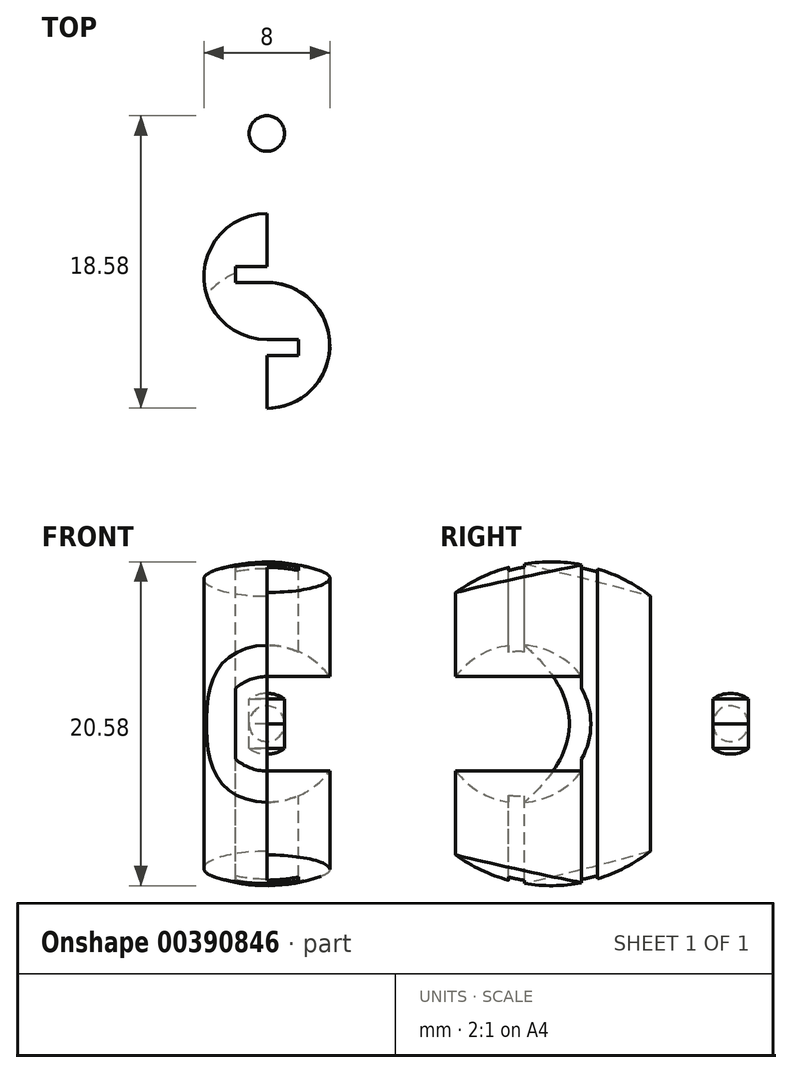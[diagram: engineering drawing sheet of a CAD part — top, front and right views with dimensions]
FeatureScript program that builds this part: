
annotation { "Feature Type Name" : "Feature", "Feature Type Description" : "" }
export const myFeature = defineFeature(function(context is Context, id is Id, definition is map)
    precondition{}
    {
        {
            var Q0;
            Q0=qCreatedBy(makeId("Top.planeOp"),FACE);
            var sketch = newSketch(context, id + "F0", { "sketchPlane" : qUnion([Q0])});
            skLineSegment(sketch, "E0", {"start": v(0, 51.88) * mm, "end": v(0, 12.79) * mm});
            skLineSegment(sketch, "E1", {"start": v(81.06, 0) * mm, "end": v(-86.12, 0) * mm, "construction": true});
            skArc(sketch, "E2", {"start": v(0, 12.79) * mm, "mid": v(-5, 7.79) * mm, "end": v(0, 2.79) * mm});
            skArc(sketch, "E3", {"start": v(0, 11.79) * mm, "mid": v(-4, 7.79) * mm, "end": v(0, 3.79) * mm});
            skArc(sketch, "E4", {"start": v(0, -1.57) * mm, "mid": v(5, 3.43) * mm, "end": v(0, 8.43) * mm});
            skArc(sketch, "E5.trimOffspring", {"start": v(0, -0.57) * mm, "mid": v(4, 3.43) * mm, "end": v(0, 7.43) * mm});
            skLineSegment(sketch, "E6", {"start": v(0, 11.79) * mm, "end": v(2, 11.79) * mm});
            skLineSegment(sketch, "E7", {"start": v(2, 11.79) * mm, "end": v(2, 12.79) * mm});
            skLineSegment(sketch, "E8", {"start": v(2, 12.79) * mm, "end": v(0, 12.79) * mm});
            skLineSegment(sketch, "E9", {"start": v(0, 3.79) * mm, "end": v(2, 3.79) * mm});
            skLineSegment(sketch, "E10", {"start": v(2, 3.79) * mm, "end": v(2, 2.79) * mm});
            skLineSegment(sketch, "E11", {"start": v(2, 2.79) * mm, "end": v(0, 2.79) * mm});
            skLineSegment(sketch, "E12", {"start": v(-2, 8.43) * mm, "end": v(0, 8.43) * mm});
            skLineSegment(sketch, "E13", {"start": v(-2, 8.43) * mm, "end": v(-2, 7.43) * mm});
            skLineSegment(sketch, "E14", {"start": v(0, 7.43) * mm, "end": v(-2, 7.43) * mm});
            skLineSegment(sketch, "E15", {"start": v(0, -0.57) * mm, "end": v(-2, -0.57) * mm});
            skLineSegment(sketch, "E16", {"start": v(-2, -0.57) * mm, "end": v(-2, -1.57) * mm});
            skLineSegment(sketch, "E17", {"start": v(0, -1.57) * mm, "end": v(-2, -1.57) * mm});
            skPoint(sketch, "E18.middle", {"position": v(0, 5.45) * mm});
            skArc(sketch, "E19", {"start": v(-1.47, 15.63) * mm, "mid": v(0, -4.83) * mm, "end": v(1.47, 15.63) * mm});
            skLineSegment(sketch, "E20.trimOffspring", {"start": v(0, 11.79) * mm, "end": v(0, 8.43) * mm});
            skLineSegment(sketch, "E21.trimOffspring", {"start": v(0, 7.43) * mm, "end": v(0, 3.79) * mm});
            skLineSegment(sketch, "E22.trimOffspring", {"start": v(0, 2.79) * mm, "end": v(0, -0.57) * mm});
            skLineSegment(sketch, "E23.trimOffspring", {"start": v(0, -1.57) * mm, "end": v(0, -69) * mm});
            skArc(sketch, "E24", {"start": v(1.47, 15.63) * mm, "mid": v(0, 18.81) * mm, "end": v(-1.47, 15.63) * mm});
            skCircle(sketch, "E25", {"center": v(0, 16.88) * mm, "radius": 1.13 * mm});
            skSolve(sketch);
        }
        {
            var Q0;
            {var subQ0=sQuery(id+"F0.wireOp",EDGE,"E4");Q0=makeQuery(id+"F0.imprint","IMPRINT",FACE,{"disambiguationData":[TD([[makeQuery(id+"F0.imprint","IMPRINT",EDGE,{"derivedFrom":subQ0}),-1.0]])]});}
            var Q1;
            Q1=sQuery(id+"F0.wireOp",EDGE,"E0");
            revolve(context, id + "F1", {"entities" : qUnion([Q0]), "axis" : qUnion([Q1]), "revolveType" : RevolveType.FULL});
        }
        {
            var Q0;
            Q0=makeQuery(id+"F0.imprint","IMPRINT",FACE,{"disambiguationData":[TD([[makeQuery(id+"F0.imprint","IMPRINT",EDGE,{"derivedFrom":sQuery(id+"F0.wireOp",EDGE,"E2")}),1.0]])]});
            var Q1;
            Q1=makeQuery(id+"F0.imprint","IMPRINT",FACE,{"disambiguationData":[TD([[makeQuery(id+"F0.imprint","IMPRINT",EDGE,{"derivedFrom":sQuery(id+"F0.wireOp",EDGE,"E4")}),1.0]])]});
            extrude(context, id + "F2", {"entities" : qUnion([Q0, Q1]), "operationType" : NewBodyOperationType.REMOVE, "oppositeDirection" : true, "depth" : 25.4 * mm, "hasSecondDirection" : true, "secondDirectionOppositeDirection" : false, "secondDirectionDepth" : 25.4 * mm});
        }
        {
            var Q0;
            {var subQ0=sQuery(id+"F0.wireOp",EDGE,"E25");var subQ1=sQuery(id+"F0.wireOp",EDGE,"E0");var subQ2=makeQuery(id+"F0.imprint","INTERSECT",VERTEX,{"disambiguationData":[OD(0.0)],"derivedFrom":[subQ1,subQ0]});Q0=makeQuery(id+"F0.imprint","IMPRINT",FACE,{"disambiguationData":[TD([[makeQuery(id+"F0.imprint","IMPRINT",EDGE,{"disambiguationData":[TD([[subQ2,-1.0]])],"derivedFrom":subQ1}),-1.0]])]});}
            var Q1;
            {var subQ0=sQuery(id+"F0.wireOp",EDGE,"E25");var subQ1=sQuery(id+"F0.wireOp",EDGE,"E0");var subQ2=makeQuery(id+"F0.imprint","INTERSECT",VERTEX,{"disambiguationData":[OD(0.0)],"derivedFrom":[subQ1,subQ0]});Q1=makeQuery(id+"F0.imprint","IMPRINT",FACE,{"disambiguationData":[TD([[makeQuery(id+"F0.imprint","IMPRINT",EDGE,{"disambiguationData":[TD([[subQ2,-1.0]])],"derivedFrom":subQ1}),1.0]])]});}
            extrude(context, id + "F3", {"entities" : qUnion([Q0, Q1]), "operationType" : NewBodyOperationType.REMOVE, "oppositeDirection" : true, "depth" : 25.4 * mm, "hasSecondDirection" : true, "secondDirectionOppositeDirection" : false, "secondDirectionDepth" : 25.4 * mm});
        }
    });
